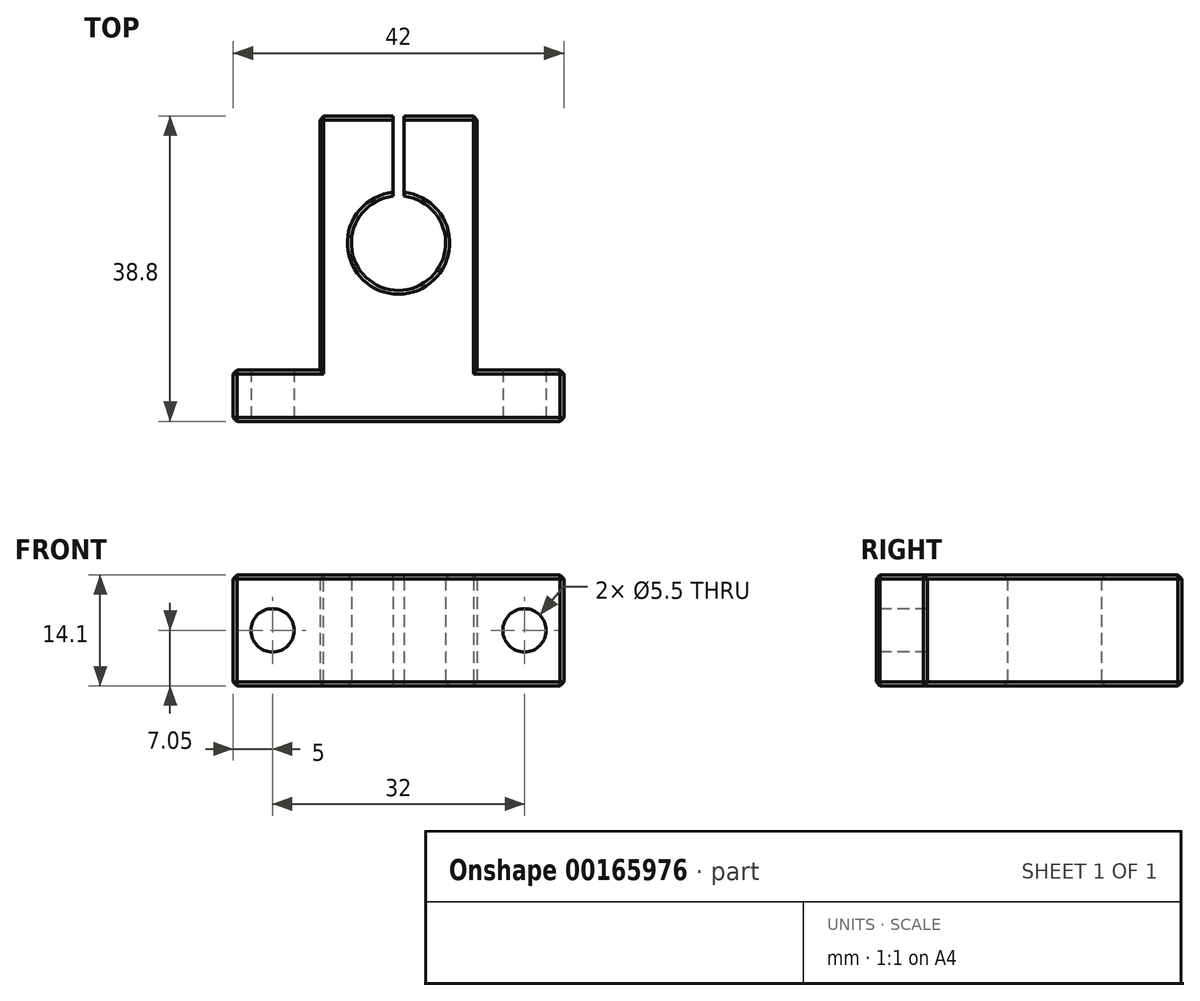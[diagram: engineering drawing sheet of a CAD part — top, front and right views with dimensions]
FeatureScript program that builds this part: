
annotation { "Feature Type Name" : "Feature", "Feature Type Description" : "" }
export const myFeature = defineFeature(function(context is Context, id is Id, definition is map)
    precondition{}
    {
        {
            var Q0;
            Q0=qCreatedBy(makeId("Top.planeOp"),FACE);
            var sketch = newSketch(context, id + "F0", { "sketchPlane" : qUnion([Q0])});
            skArc(sketch, "E0", {"start": v(-0.68, 4.81) * mm, "mid": v(0, -7.15) * mm, "end": v(0.67, 4.81) * mm});
            skLineSegment(sketch, "E1.top", {"start": v(10, 15) * mm, "end": v(0.67, 15) * mm});
            skLineSegment(sketch, "E1.left", {"start": v(10, -17.3) * mm, "end": v(10, 15) * mm});
            skLineSegment(sketch, "E1.right", {"start": v(-10, -17.3) * mm, "end": v(-10, 15) * mm});
            skLineSegment(sketch, "E2.bottom", {"start": v(21, -23.8) * mm, "end": v(-21, -23.8) * mm});
            skLineSegment(sketch, "E2.top", {"start": v(21, -17.3) * mm, "end": v(10, -17.3) * mm});
            skLineSegment(sketch, "E2.left", {"start": v(21, -23.8) * mm, "end": v(21, -17.3) * mm});
            skLineSegment(sketch, "E2.right", {"start": v(-21, -23.8) * mm, "end": v(-21, -17.3) * mm});
            skPoint(sketch, "E2.middle", {"position": v(0, -20.55) * mm});
            skLineSegment(sketch, "E3.trimOffspring", {"start": v(-10, -17.3) * mm, "end": v(-21, -17.3) * mm});
            skLineSegment(sketch, "E4.left", {"start": v(0.67, 4.81) * mm, "end": v(0.67, 15) * mm});
            skLineSegment(sketch, "E4.right", {"start": v(-0.68, 4.81) * mm, "end": v(-0.68, 15) * mm});
            skPoint(sketch, "E4.middle", {"position": v(0, 15) * mm});
            skPoint(sketch, "E4.top.start.orphan", {"position": v(0.67, 25.5) * mm});
            skPoint(sketch, "E5.orphan", {"position": v(-0.68, 25.5) * mm});
            skPoint(sketch, "E6.orphan", {"position": v(-0.68, 4.5) * mm});
            skPoint(sketch, "E7.orphan", {"position": v(0.67, 4.5) * mm});
            skLineSegment(sketch, "E8.trimOffspring", {"start": v(-0.68, 15) * mm, "end": v(-10, 15) * mm});
            skSolve(sketch);
        }
        {
            var Q0;
            Q0 = qSketchRegion(id + "F0", true);
            extrude(context, id + "F1", {"entities" : qUnion([Q0]), "depth" : 14.1 * mm});
        }
        {
            var Q0;
            Q0=makeQuery(id+"F1.opExtrude","SWEPT_FACE",FACE,{"disambiguationData":[OSD([sQuery(id+"F0.wireOp",EDGE,"E2.bottom")])]});
            var sketch = newSketch(context, id + "F2", { "sketchPlane" : qUnion([Q0])});
            skCircle(sketch, "E9", {"center": v(16, 7.05) * mm, "radius": 2.75 * mm});
            skPoint(sketch, "E9.centerSnap0", {"position": v(21, 7.05) * mm});
            skCircle(sketch, "E10.MirrorC", {"center": v(-16, 7.05) * mm, "radius": 2.75 * mm});
            skSolve(sketch);
        }
        {
            var Q0;
            Q0 = qSketchRegion(id + "F2", true);
            extrude(context, id + "F3", {"entities" : qUnion([Q0]), "operationType" : NewBodyOperationType.REMOVE, "endBound" : BoundingType.THROUGH_ALL, "oppositeDirection" : true, "depth" : 25 * mm});
        }
        {
            var Q0;
            Q0=makeQuery(id+"F1.opExtrude","CAP_EDGE",EDGE,{"disambiguationData":[OSD([sQuery(id+"F0.wireOp",EDGE,"E1.left")])],"isStart":false});
            var Q1;
            Q1=makeQuery(id+"F1.opExtrude","CAP_EDGE",EDGE,{"disambiguationData":[OSD([sQuery(id+"F0.wireOp",EDGE,"E2.top")])],"isStart":false});
            var Q2;
            Q2=makeQuery(id+"F1.opExtrude","CAP_EDGE",EDGE,{"disambiguationData":[OSD([sQuery(id+"F0.wireOp",EDGE,"E2.left")])],"isStart":false});
            var Q3;
            Q3=makeQuery(id+"F1.opExtrude","SWEPT_EDGE",EDGE,{"disambiguationData":[OSD([sQuery(id+"F0.wireOp",EDGE,"E2.top"),sQuery(id+"F0.wireOp",EDGE,"E2.left")])]});
            var Q4;
            Q4=makeQuery(id+"F1.opExtrude","SWEPT_EDGE",EDGE,{"disambiguationData":[OSD([sQuery(id+"F0.wireOp",EDGE,"E2.bottom"),sQuery(id+"F0.wireOp",EDGE,"E2.left")])]});
            var Q5;
            Q5=makeQuery(id+"F1.opExtrude","CAP_EDGE",EDGE,{"disambiguationData":[OSD([sQuery(id+"F0.wireOp",EDGE,"E2.left")])],"isStart":true});
            var Q6;
            Q6=makeQuery(id+"F1.opExtrude","CAP_EDGE",EDGE,{"disambiguationData":[OSD([sQuery(id+"F0.wireOp",EDGE,"E2.bottom")])],"isStart":false});
            var Q7;
            Q7=makeQuery(id+"F1.opExtrude","CAP_EDGE",EDGE,{"disambiguationData":[OSD([sQuery(id+"F0.wireOp",EDGE,"E3.trimOffspring")])],"isStart":false});
            var Q8;
            Q8=makeQuery(id+"F1.opExtrude","CAP_EDGE",EDGE,{"disambiguationData":[OSD([sQuery(id+"F0.wireOp",EDGE,"E2.right")])],"isStart":false});
            var Q9;
            Q9=makeQuery(id+"F1.opExtrude","CAP_EDGE",EDGE,{"disambiguationData":[OSD([sQuery(id+"F0.wireOp",EDGE,"E1.right")])],"isStart":false});
            var Q10;
            Q10=makeQuery(id+"F1.opExtrude","CAP_EDGE",EDGE,{"disambiguationData":[OSD([sQuery(id+"F0.wireOp",EDGE,"E8.trimOffspring")])],"isStart":false});
            var Q11;
            Q11=makeQuery(id+"F1.opExtrude","CAP_EDGE",EDGE,{"disambiguationData":[OSD([sQuery(id+"F0.wireOp",EDGE,"E1.top")])],"isStart":false});
            var Q12;
            Q12=makeQuery(id+"F1.opExtrude","CAP_EDGE",EDGE,{"disambiguationData":[OSD([sQuery(id+"F0.wireOp",EDGE,"E0")])],"isStart":false});
            var Q13;
            Q13=makeQuery(id+"F1.opExtrude","SWEPT_EDGE",EDGE,{"disambiguationData":[OSD([sQuery(id+"F0.wireOp",EDGE,"E2.right"),sQuery(id+"F0.wireOp",EDGE,"E3.trimOffspring")])]});
            var Q14;
            Q14=makeQuery(id+"F1.opExtrude","SWEPT_EDGE",EDGE,{"disambiguationData":[OSD([sQuery(id+"F0.wireOp",EDGE,"E2.bottom"),sQuery(id+"F0.wireOp",EDGE,"E2.right")])]});
            var Q15;
            Q15=makeQuery(id+"F1.opExtrude","CAP_EDGE",EDGE,{"disambiguationData":[OSD([sQuery(id+"F0.wireOp",EDGE,"E2.right")])],"isStart":true});
            var Q16;
            Q16=makeQuery(id+"F1.opExtrude","CAP_EDGE",EDGE,{"disambiguationData":[OSD([sQuery(id+"F0.wireOp",EDGE,"E3.trimOffspring")])],"isStart":true});
            var Q17;
            Q17=makeQuery(id+"F1.opExtrude","CAP_EDGE",EDGE,{"disambiguationData":[OSD([sQuery(id+"F0.wireOp",EDGE,"E1.right")])],"isStart":true});
            var Q18;
            Q18=makeQuery(id+"F1.opExtrude","CAP_EDGE",EDGE,{"disambiguationData":[OSD([sQuery(id+"F0.wireOp",EDGE,"E2.bottom")])],"isStart":true});
            var Q19;
            Q19=makeQuery(id+"F1.opExtrude","CAP_EDGE",EDGE,{"disambiguationData":[OSD([sQuery(id+"F0.wireOp",EDGE,"E0")])],"isStart":true});
            var Q20;
            Q20=makeQuery(id+"F1.opExtrude","SWEPT_EDGE",EDGE,{"disambiguationData":[OSD([sQuery(id+"F0.wireOp",EDGE,"E1.right"),sQuery(id+"F0.wireOp",EDGE,"E8.trimOffspring")])]});
            var Q21;
            Q21=makeQuery(id+"F1.opExtrude","CAP_EDGE",EDGE,{"disambiguationData":[OSD([sQuery(id+"F0.wireOp",EDGE,"E8.trimOffspring")])],"isStart":true});
            var Q22;
            Q22=makeQuery(id+"F1.opExtrude","CAP_EDGE",EDGE,{"disambiguationData":[OSD([sQuery(id+"F0.wireOp",EDGE,"E1.top")])],"isStart":true});
            var Q23;
            Q23=makeQuery(id+"F1.opExtrude","CAP_EDGE",EDGE,{"disambiguationData":[OSD([sQuery(id+"F0.wireOp",EDGE,"E1.left")])],"isStart":true});
            var Q24;
            Q24=makeQuery(id+"F1.opExtrude","CAP_EDGE",EDGE,{"disambiguationData":[OSD([sQuery(id+"F0.wireOp",EDGE,"E2.top")])],"isStart":true});
            var Q25;
            Q25=makeQuery(id+"F1.opExtrude","SWEPT_EDGE",EDGE,{"disambiguationData":[OSD([sQuery(id+"F0.wireOp",EDGE,"E1.top"),sQuery(id+"F0.wireOp",EDGE,"E1.left")])]});
            chamfer(context, id + "F4", {"entities" : qUnion([Q0, Q1, Q2, Q3, Q4, Q5, Q6, Q7, Q8, Q9, Q10, Q11, Q12, Q13, Q14, Q15, Q16, Q17, Q18, Q19, Q20, Q21, Q22, Q23, Q24, Q25]), "width" : .5 * mm, "tangentPropagation" : true});
        }
    });
